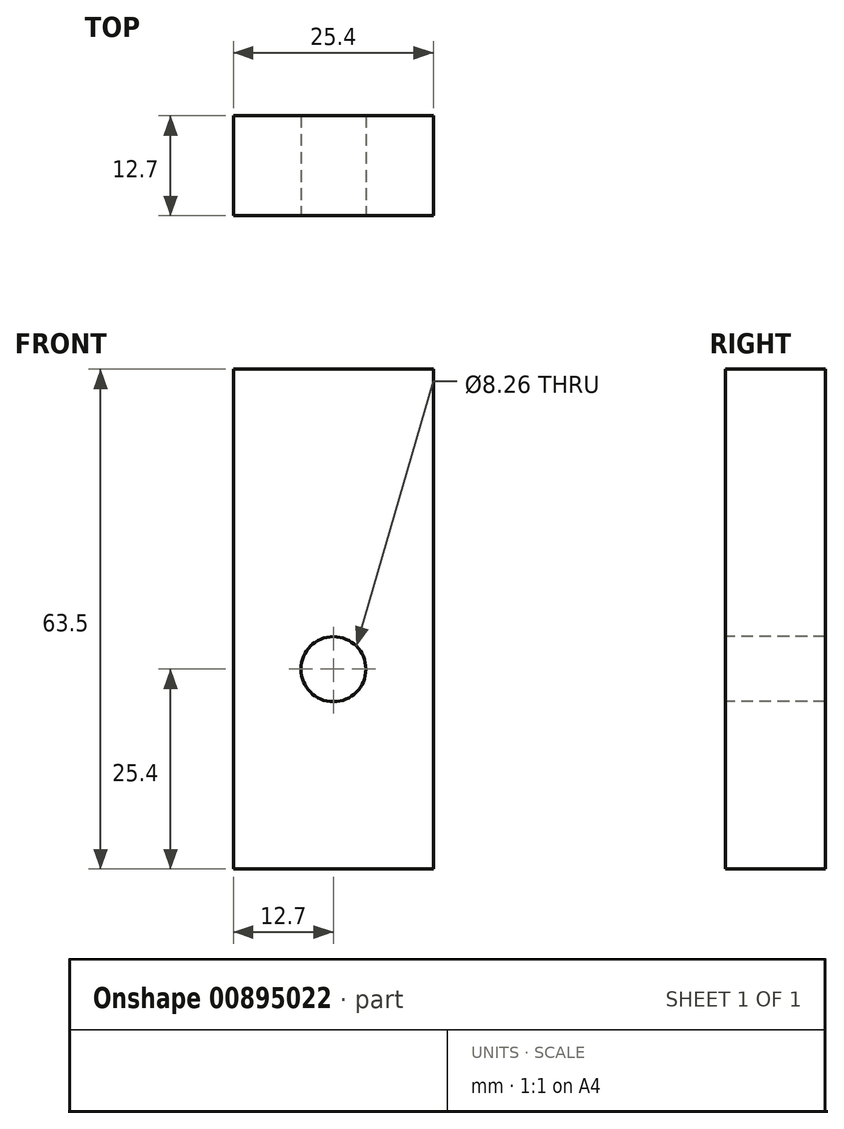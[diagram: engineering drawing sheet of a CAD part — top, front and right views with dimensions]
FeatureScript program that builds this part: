
annotation { "Feature Type Name" : "Feature", "Feature Type Description" : "" }
export const myFeature = defineFeature(function(context is Context, id is Id, definition is map)
    precondition{}
    {
        {
            var Q0;
            Q0=qCreatedBy(makeId("Top.planeOp"),FACE);
            var sketch = newSketch(context, id + "F0", { "sketchPlane" : qUnion([Q0])});
            skLineSegment(sketch, "E0.bottom", {"start": v(-2.89, 22.78) * mm, "end": v(22.51, 22.78) * mm});
            skLineSegment(sketch, "E0.top", {"start": v(-2.89, 10.08) * mm, "end": v(22.51, 10.08) * mm});
            skLineSegment(sketch, "E0.left", {"start": v(-2.89, 22.78) * mm, "end": v(-2.89, 10.08) * mm});
            skLineSegment(sketch, "E0.right", {"start": v(22.51, 22.78) * mm, "end": v(22.51, 10.08) * mm});
            skSolve(sketch);
        }
        {
            var Q0;
            Q0 = qSketchRegion(id + "F0", true);
            extrude(context, id + "F1", {"entities" : qUnion([Q0]), "depth" : 63.5 * mm, "offsetDistance" : 25.4 * mm});
        }
        {
            var Q0;
            Q0=makeQuery(id+"F1.opExtrude","SWEPT_FACE",FACE,{"disambiguationData":[OSD([sQuery(id+"F0.wireOp",EDGE,"E0.top")])]});
            var sketch = newSketch(context, id + "F2", { "sketchPlane" : qUnion([Q0])});
            skCircle(sketch, "E1", {"center": v(9.81, 25.4) * mm, "radius": 4.13 * mm});
            skPoint(sketch, "E1.centerSnap0", {"position": v(9.81, 63.5) * mm});
            skSolve(sketch);
        }
        {
            var Q0;
            Q0 = qSketchRegion(id + "F2", true);
            extrude(context, id + "F3", {"entities" : qUnion([Q0]), "operationType" : NewBodyOperationType.REMOVE, "oppositeDirection" : true, "depth" : 25.4 * mm, "offsetDistance" : 25.4 * mm});
        }
    });
